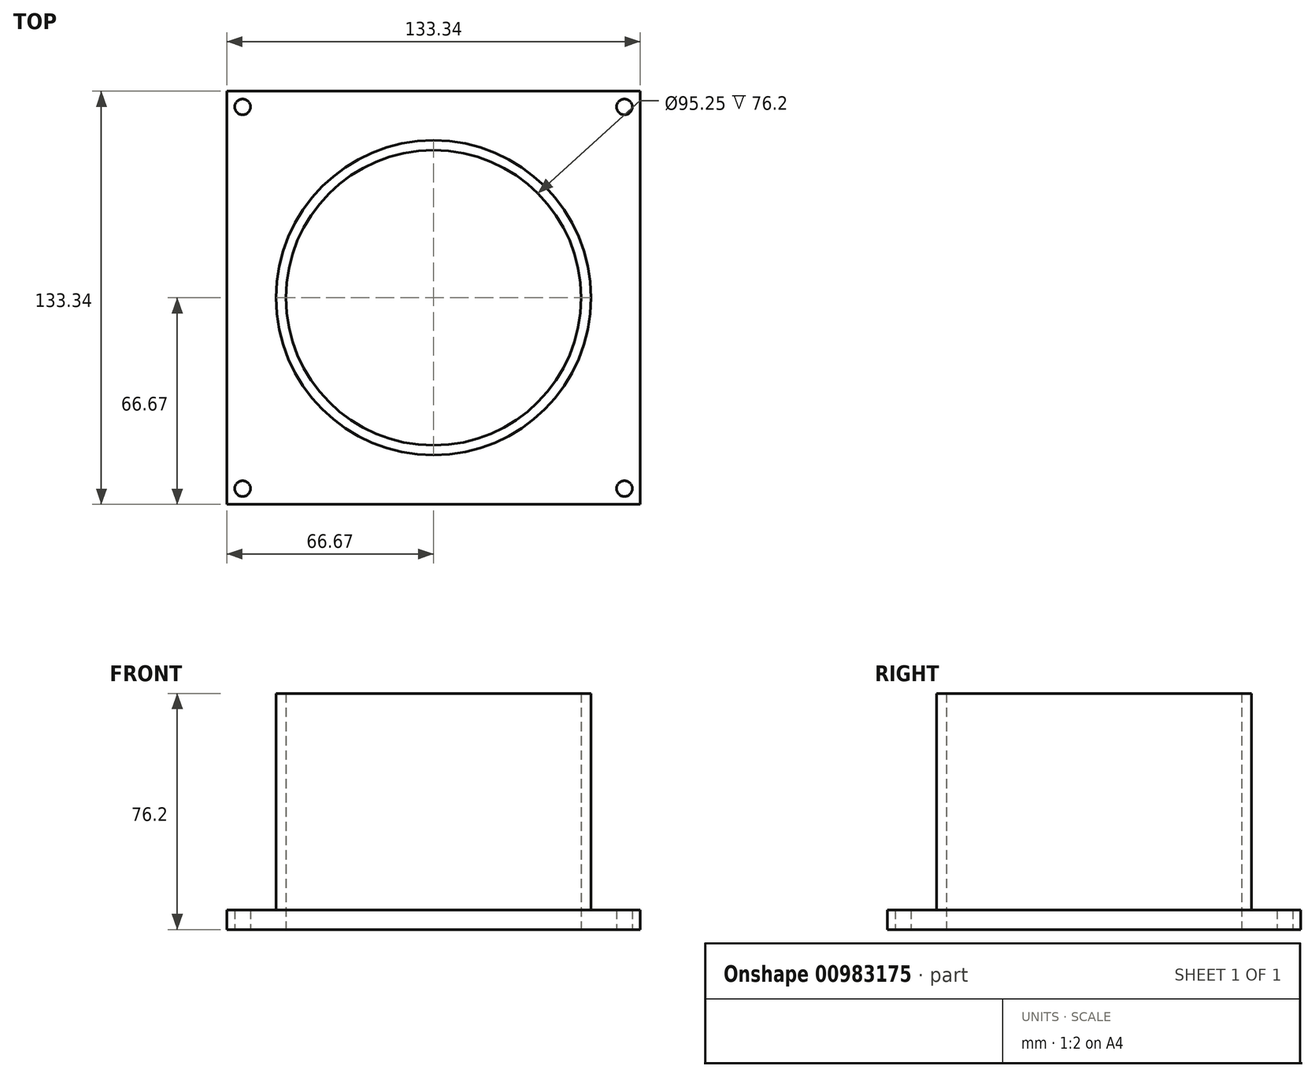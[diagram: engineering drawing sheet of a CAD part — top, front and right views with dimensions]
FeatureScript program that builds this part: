
annotation { "Feature Type Name" : "Feature", "Feature Type Description" : "" }
export const myFeature = defineFeature(function(context is Context, id is Id, definition is map)
    precondition{}
    {
        {
            var Q0;
            Q0=qCreatedBy(makeId("Top.planeOp"),FACE);
            var sketch = newSketch(context, id + "F0", { "sketchPlane" : qUnion([Q0])});
            skLineSegment(sketch, "E0.bottom", {"start": v(-66.67, 66.68) * mm, "end": v(66.68, 66.68) * mm});
            skLineSegment(sketch, "E0.top", {"start": v(-66.68, -66.68) * mm, "end": v(66.67, -66.68) * mm});
            skLineSegment(sketch, "E0.left", {"start": v(-66.67, 66.68) * mm, "end": v(-66.68, -66.67) * mm});
            skLineSegment(sketch, "E0.right", {"start": v(66.68, 66.68) * mm, "end": v(66.67, -66.67) * mm});
            skPoint(sketch, "E0.middle", {"position": v(0, 0) * mm});
            skCircle(sketch, "E1", {"center": v(-61.6, 61.6) * mm, "radius": 2.54 * mm});
            skCircle(sketch, "E2", {"center": v(61.6, 61.6) * mm, "radius": 2.54 * mm});
            skCircle(sketch, "E3", {"center": v(-61.6, -61.6) * mm, "radius": 2.54 * mm});
            skCircle(sketch, "E4", {"center": v(61.6, -61.6) * mm, "radius": 2.54 * mm});
            skCircle(sketch, "E5", {"center": v(0, 0) * mm, "radius": 50.8 * mm});
            skCircle(sketch, "E6", {"center": v(0, 0) * mm, "radius": 47.63 * mm});
            skSolve(sketch);
        }
        {
            var Q0;
            Q0=makeQuery(id+"F0.imprint","IMPRINT",FACE,{"disambiguationData":[TD([[makeQuery(id+"F0.imprint","IMPRINT",EDGE,{"derivedFrom":sQuery(id+"F0.wireOp",EDGE,"E5")}),1.0]])]});
            extrude(context, id + "F1", {"entities" : qUnion([Q0]), "depth" : 76.2 * mm, "offsetDistance" : 25.4 * mm});
        }
        {
            var Q0;
            Q0=qSketchRegion(id+"F0",true);
            extrude(context, id + "F2", {"entities" : qUnion([Q0]), "operationType" : NewBodyOperationType.ADD, "depth" : 6.35 * mm, "offsetDistance" : 25.4 * mm});
        }
    });
